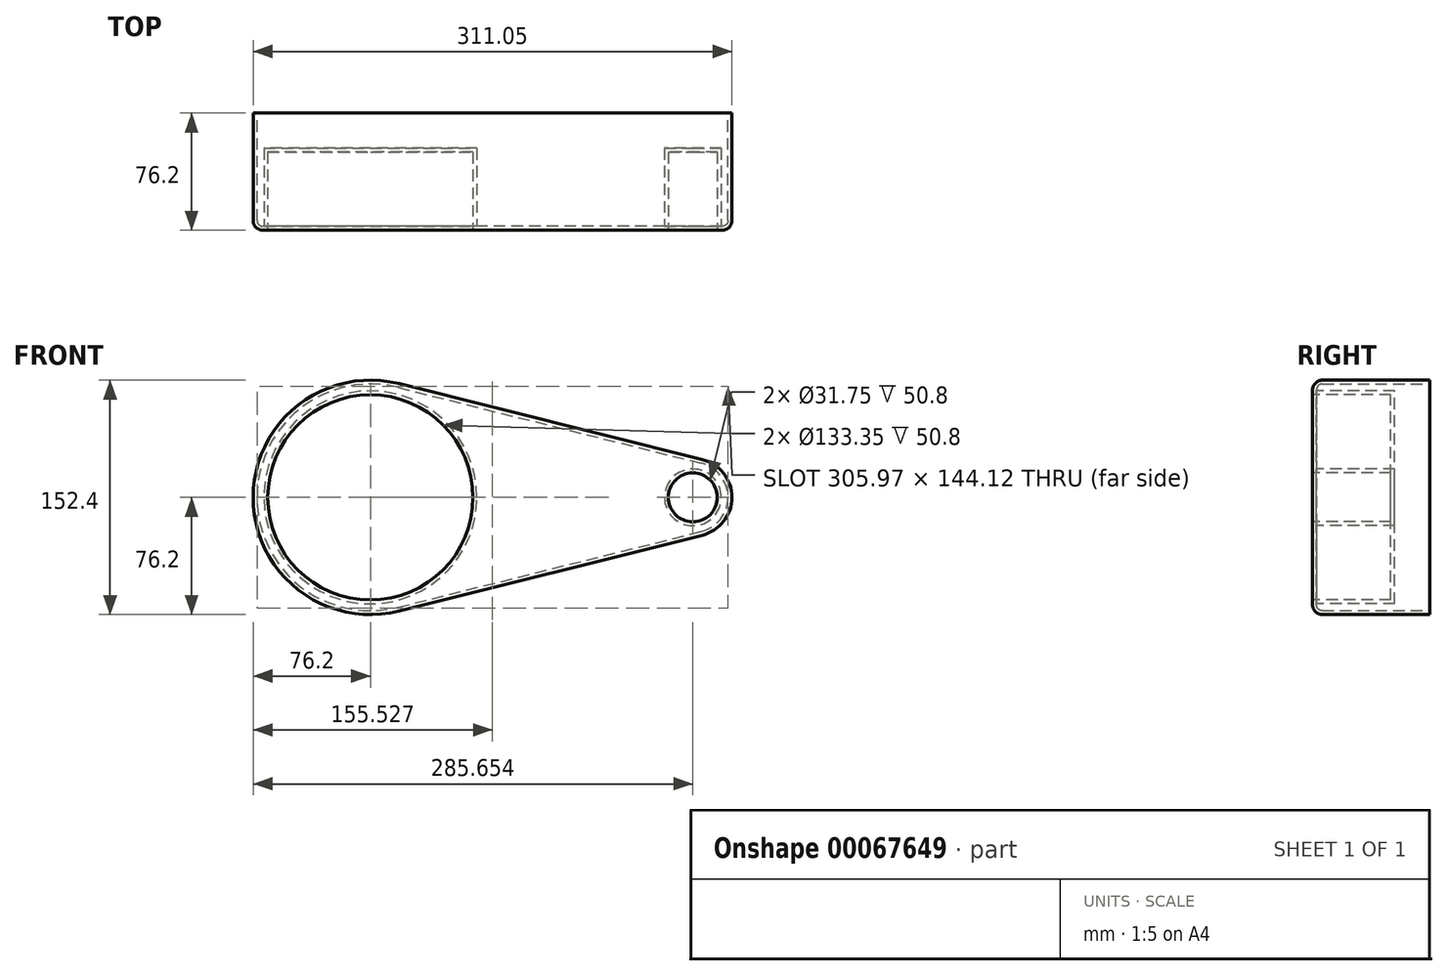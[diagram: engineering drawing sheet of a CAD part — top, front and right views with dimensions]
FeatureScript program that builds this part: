
annotation { "Feature Type Name" : "Feature", "Feature Type Description" : "" }
export const myFeature = defineFeature(function(context is Context, id is Id, definition is map)
    precondition{}
    {
        {
            var Q0;
            Q0=qCreatedBy(makeId("Front.planeOp"),FACE);
            var sketch = newSketch(context, id + "F0", { "sketchPlane" : qUnion([Q0])});
            skCircle(sketch, "E0", {"center": v(0, 0) * mm, "radius": 76.2 * mm});
            skCircle(sketch, "E1", {"center": v(209.45, 0) * mm, "radius": 25.4 * mm});
            skLineSegment(sketch, "E2", {"start": v(18.48, 73.92) * mm, "end": v(215.61, 24.64) * mm});
            skLineSegment(sketch, "E3", {"start": v(18.48, -73.92) * mm, "end": v(215.61, -24.64) * mm});
            skSolve(sketch);
        }
        {
            var Q0;
            {var subQ0=sQuery(id+"F0.wireOp",EDGE,"E0");var subQ1=makeQuery(id+"F0.imprint","INTERSECT",VERTEX,{"derivedFrom":[subQ0,sQuery(id+"F0.wireOp",EDGE,"E2")]});Q0=makeQuery(id+"F0.imprint","IMPRINT",FACE,{"disambiguationData":[TD([[makeQuery(id+"F0.imprint","IMPRINT",EDGE,{"disambiguationData":[TD([[subQ1,-1.0]])],"derivedFrom":subQ0}),1.0]])]});}
            var Q1;
            {var subQ0=sQuery(id+"F0.wireOp",EDGE,"E2");Q1=makeQuery(id+"F0.imprint","IMPRINT",FACE,{"disambiguationData":[TD([[makeQuery(id+"F0.imprint","IMPRINT",EDGE,{"derivedFrom":subQ0}),-1.0]])]});}
            var Q2;
            {var subQ0=sQuery(id+"F0.wireOp",EDGE,"E1");var subQ1=makeQuery(id+"F0.imprint","INTERSECT",VERTEX,{"derivedFrom":[subQ0,sQuery(id+"F0.wireOp",EDGE,"E2")]});Q2=makeQuery(id+"F0.imprint","IMPRINT",FACE,{"disambiguationData":[TD([[makeQuery(id+"F0.imprint","IMPRINT",EDGE,{"disambiguationData":[TD([[subQ1,-1.0]])],"derivedFrom":subQ0}),1.0]])]});}
            extrude(context, id + "F1", {"entities" : qUnion([Q0, Q1, Q2]), "depth" : 76.2 * mm});
        }
        {
            var Q0;
            Q0=makeQuery(id+"F1.opExtrude","CAP_FACE",FACE,{"disambiguationData":[OSD([sQuery(id+"F0.wireOp",EDGE,"E0"),sQuery(id+"F0.wireOp",EDGE,"E1"),sQuery(id+"F0.wireOp",EDGE,"E2"),sQuery(id+"F0.wireOp",EDGE,"E3")])],"isStart":false});
            var sketch = newSketch(context, id + "F2", { "sketchPlane" : qUnion([Q0])});
            skCircle(sketch, "E4", {"center": v(0, 0) * mm, "radius": 66.68 * mm});
            skCircle(sketch, "E5", {"center": v(209.45, 0) * mm, "radius": 15.88 * mm});
            skSolve(sketch);
        }
        {
            var Q0;
            Q0=makeQuery(id+"F2.imprint","IMPRINT",FACE,{"disambiguationData":[TD([[makeQuery(id+"F2.imprint","IMPRINT",EDGE,{"derivedFrom":sQuery(id+"F2.wireOp",EDGE,"E4")}),1.0]])]});
            var Q1;
            Q1=makeQuery(id+"F2.imprint","IMPRINT",FACE,{"disambiguationData":[TD([[makeQuery(id+"F2.imprint","IMPRINT",EDGE,{"derivedFrom":sQuery(id+"F2.wireOp",EDGE,"E5")}),1.0]])]});
            extrude(context, id + "F3", {"entities" : qUnion([Q0, Q1]), "operationType" : NewBodyOperationType.REMOVE, "oppositeDirection" : true, "depth" : 50.8 * mm});
        }
        {
            var Q0;
            Q0=makeQuery(id+"F1.opExtrude","CAP_EDGE",EDGE,{"disambiguationData":[OSD([sQuery(id+"F0.wireOp",EDGE,"E0")])],"isStart":false});
            var Q1;
            Q1=makeQuery(id+"F3.boolean.opBoolean","COPY",EDGE,{"derivedFrom":makeQuery(id+"F3.opExtrude","CAP_EDGE",EDGE,{"disambiguationData":[OSD([sQuery(id+"F2.wireOp",EDGE,"E4")])],"isStart":true})});
            var Q2;
            Q2=makeQuery(id+"F1.opExtrude","CAP_EDGE",EDGE,{"disambiguationData":[OSD([sQuery(id+"F0.wireOp",EDGE,"E2")])],"isStart":false});
            var Q3;
            Q3=makeQuery(id+"F1.opExtrude","CAP_EDGE",EDGE,{"disambiguationData":[OSD([sQuery(id+"F0.wireOp",EDGE,"E3")])],"isStart":false});
            var Q4;
            Q4=makeQuery(id+"F3.boolean.opBoolean","COPY",EDGE,{"derivedFrom":makeQuery(id+"F3.opExtrude","CAP_EDGE",EDGE,{"disambiguationData":[OSD([sQuery(id+"F2.wireOp",EDGE,"E5")])],"isStart":true})});
            var Q5;
            Q5=makeQuery(id+"F1.opExtrude","CAP_EDGE",EDGE,{"disambiguationData":[OSD([sQuery(id+"F0.wireOp",EDGE,"E1")])],"isStart":false});
            fillet(context, id + "F4", {"entities" : qUnion([Q0, Q1, Q2, Q3, Q4, Q5]), "radius" : 6.35 * mm, "tangentPropagation" : true, "allowEdgeOverflow" : false});
        }
        {
            var Q0;
            Q0=makeQuery(id+"F1.opExtrude","CAP_FACE",FACE,{"disambiguationData":[OSD([sQuery(id+"F0.wireOp",EDGE,"E0"),sQuery(id+"F0.wireOp",EDGE,"E1"),sQuery(id+"F0.wireOp",EDGE,"E2"),sQuery(id+"F0.wireOp",EDGE,"E3")])],"isStart":true});
            shell(context, id + "F5", {"entities" : qUnion([Q0]), "thickness" : 2.54 * mm});
        }
    });
